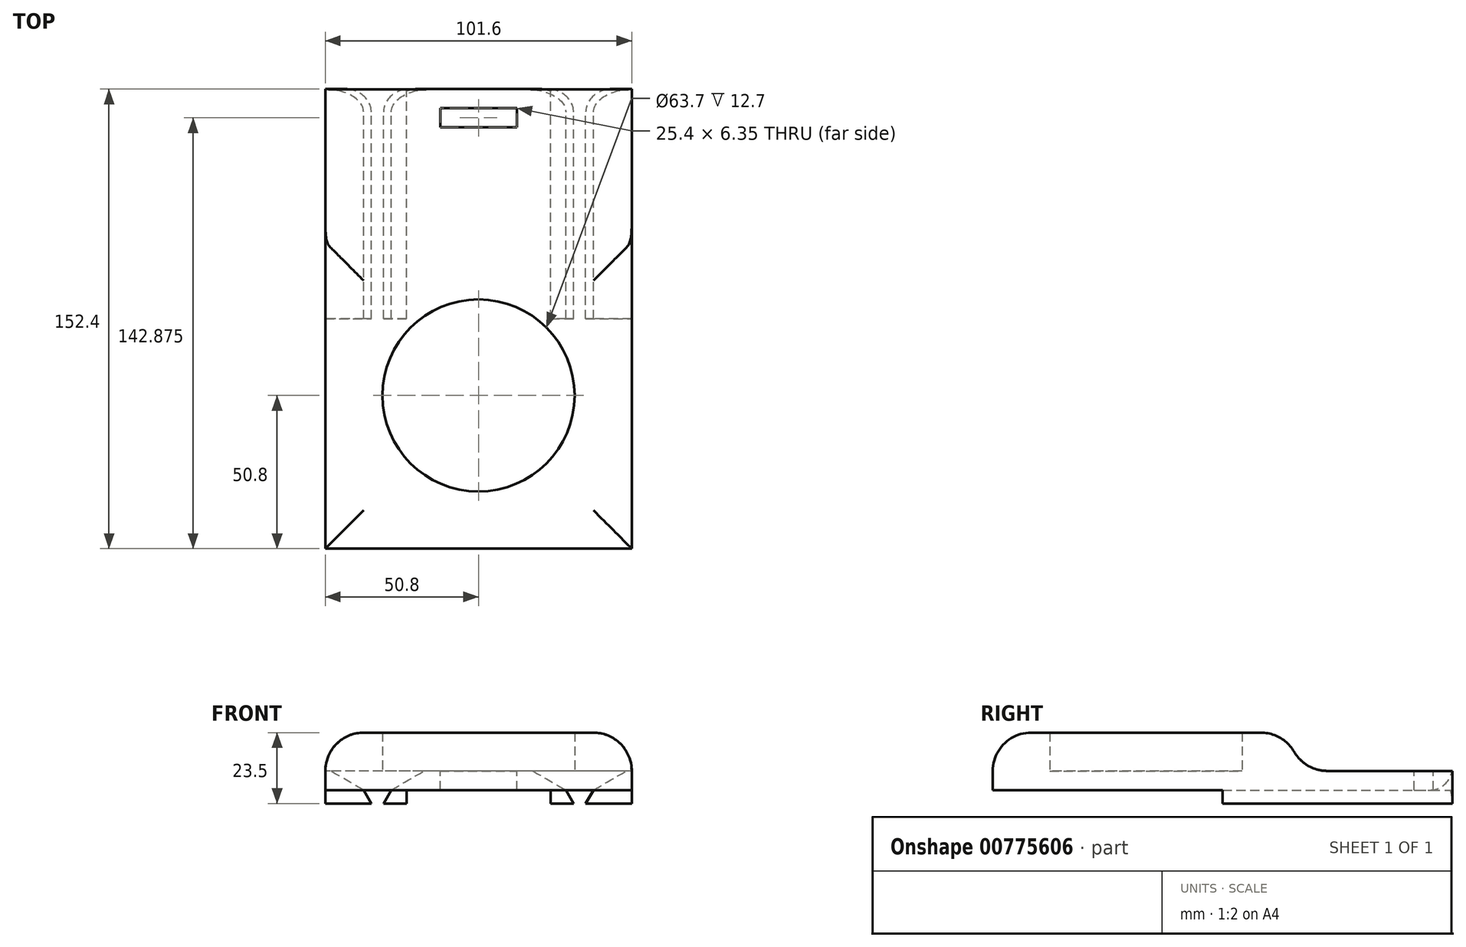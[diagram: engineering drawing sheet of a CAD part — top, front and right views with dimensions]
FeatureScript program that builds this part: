
annotation { "Feature Type Name" : "Feature", "Feature Type Description" : "" }
export const myFeature = defineFeature(function(context is Context, id is Id, definition is map)
    precondition{}
    {
        {
            var Q0;
            Q0=qCreatedBy(makeId("Top.planeOp"),FACE);
            var sketch = newSketch(context, id + "F0", { "sketchPlane" : qUnion([Q0])});
            skLineSegment(sketch, "E0.bottom", {"start": v(50.8, -76.2) * mm, "end": v(-50.8, -76.2) * mm});
            skLineSegment(sketch, "E0.top", {"start": v(50.8, 76.2) * mm, "end": v(-50.8, 76.2) * mm});
            skLineSegment(sketch, "E0.left", {"start": v(50.8, -76.2) * mm, "end": v(50.8, 76.2) * mm});
            skLineSegment(sketch, "E0.right", {"start": v(-50.8, -76.2) * mm, "end": v(-50.8, 76.2) * mm});
            skPoint(sketch, "E0.middle", {"position": v(0, 0) * mm});
            skSolve(sketch);
        }
        {
            var Q0;
            Q0 = qSketchRegion(id + "F0", true);
            extrude(context, id + "F1", {"entities" : qUnion([Q0]), "depth" : 6.35 * mm, "offsetDistance" : 25.4 * mm});
        }
        {
            var Q0;
            Q0=makeQuery(id+"F1.opExtrude","CAP_FACE",FACE,{"disambiguationData":[OSD([sQuery(id+"F0.wireOp",EDGE,"E0.bottom"),sQuery(id+"F0.wireOp",EDGE,"E0.top"),sQuery(id+"F0.wireOp",EDGE,"E0.left"),sQuery(id+"F0.wireOp",EDGE,"E0.right")])],"isStart":false});
            var sketch = newSketch(context, id + "F2", { "sketchPlane" : qUnion([Q0])});
            skLineSegment(sketch, "E1.bottom", {"start": v(-12.7, 69.85) * mm, "end": v(12.7, 69.85) * mm});
            skLineSegment(sketch, "E1.top", {"start": v(-12.7, 63.5) * mm, "end": v(12.7, 63.5) * mm});
            skLineSegment(sketch, "E1.left", {"start": v(-12.7, 69.85) * mm, "end": v(-12.7, 63.5) * mm});
            skLineSegment(sketch, "E1.right", {"start": v(12.7, 69.85) * mm, "end": v(12.7, 63.5) * mm});
            skLineSegment(sketch, "E2", {"start": v(0, -76.2) * mm, "end": v(0, 76.2) * mm});
            skSolve(sketch);
        }
        {
            var Q0;
            Q0 = qSketchRegion(id + "F2", true);
            extrude(context, id + "F3", {"entities" : qUnion([Q0]), "operationType" : NewBodyOperationType.REMOVE, "endBound" : BoundingType.UP_TO_NEXT, "oppositeDirection" : true, "depth" : 25.4 * mm, "offsetDistance" : 25.4 * mm});
        }
        {
            var Q0;
            Q0=makeQuery(id+"F1.opExtrude","SWEPT_FACE",FACE,{"disambiguationData":[OSD([sQuery(id+"F0.wireOp",EDGE,"E0.top")])]});
            var sketch = newSketch(context, id + "F4", { "sketchPlane" : qUnion([Q0])});
            skLineSegment(sketch, "E3", {"start": v(38.1, 0) * mm, "end": v(50.8, 0) * mm});
            skLineSegment(sketch, "E4", {"start": v(50.8, 0) * mm, "end": v(50.8, -4.44) * mm});
            skLineSegment(sketch, "E5", {"start": v(50.8, -4.44) * mm, "end": v(35.53, -4.44) * mm});
            skLineSegment(sketch, "E6", {"start": v(35.53, -4.45) * mm, "end": v(38.1, 0) * mm});
            skLineSegment(sketch, "E7", {"start": v(31.52, -4.44) * mm, "end": v(23.88, -4.45) * mm});
            skLineSegment(sketch, "E8", {"start": v(23.88, -4.45) * mm, "end": v(23.88, 0) * mm});
            skLineSegment(sketch, "E9", {"start": v(23.88, 0) * mm, "end": v(28.96, 0) * mm});
            skLineSegment(sketch, "E10", {"start": v(28.96, 0) * mm, "end": v(31.52, -4.45) * mm});
            skLineSegment(sketch, "E11", {"start": v(-23.88, 0) * mm, "end": v(-23.88, -4.45) * mm});
            skLineSegment(sketch, "E12", {"start": v(-23.88, -4.45) * mm, "end": v(-31.52, -4.45) * mm});
            skLineSegment(sketch, "E13", {"start": v(-31.52, -4.45) * mm, "end": v(-28.96, 0) * mm});
            skLineSegment(sketch, "E14", {"start": v(-28.96, 0) * mm, "end": v(-23.88, 0) * mm});
            skLineSegment(sketch, "E15", {"start": v(-35.53, -4.45) * mm, "end": v(-50.8, -4.45) * mm});
            skLineSegment(sketch, "E16", {"start": v(-50.8, -4.45) * mm, "end": v(-50.8, 0) * mm});
            skLineSegment(sketch, "E17", {"start": v(-50.8, 0) * mm, "end": v(-38.1, 0) * mm});
            skLineSegment(sketch, "E18", {"start": v(-38.1, 0) * mm, "end": v(-35.53, -4.45) * mm});
            skSolve(sketch);
        }
        {
            var Q0;
            Q0 = qSketchRegion(id + "F4", true);
            extrude(context, id + "F5", {"entities" : qUnion([Q0]), "operationType" : NewBodyOperationType.ADD, "oppositeDirection" : true, "depth" : 76.2 * mm, "offsetDistance" : 25.4 * mm});
        }
        {
            var Q0;
            Q0=makeQuery(id+"F5.opExtrude","CAP_EDGE",EDGE,{"disambiguationData":[OSD([sQuery(id+"F4.wireOp",EDGE,"E10")])],"isStart":true});
            var Q1;
            Q1=makeQuery(id+"F5.opExtrude","CAP_EDGE",EDGE,{"disambiguationData":[OSD([sQuery(id+"F4.wireOp",EDGE,"E6")])],"isStart":true});
            var Q2;
            {var subQ0=sQuery(id+"F4.wireOp",EDGE,"E6");var subQ1=sQuery(id+"F0.wireOp",EDGE,"E0.top");Q2=makeQuery(id+"F5.boolean.opBoolean","SPLIT",EDGE,{"disambiguationData":[TD([makeQuery(id+"F5.opExtrude","SWEPT_FACE",FACE,{"disambiguationData":[OSD([subQ0])]})])],"derivedFrom":makeQuery(id+"F1.opExtrude","CAP_EDGE",EDGE,{"disambiguationData":[OSD([subQ1])],"isStart":true})});}
            fillet(context, id + "F6", {"entities" : qUnion([Q0, Q1, Q2]), "radius" : 7.62 * mm, "tangentPropagation" : true, "allowEdgeOverflow" : false});
        }
        {
            var Q0;
            Q0=makeQuery(id+"F5.opExtrude","CAP_EDGE",EDGE,{"disambiguationData":[OSD([sQuery(id+"F4.wireOp",EDGE,"E18")])],"isStart":true});
            var Q1;
            {var subQ1=sQuery(id+"F0.wireOp",EDGE,"E0.top");var subQ2=sQuery(id+"F4.wireOp",EDGE,"E13");Q1=makeQuery(id+"F5.boolean.opBoolean","SPLIT",EDGE,{"disambiguationData":[TD([makeQuery(id+"F5.opExtrude","SWEPT_FACE",FACE,{"disambiguationData":[OSD([subQ2])]})])],"derivedFrom":makeQuery(id+"F1.opExtrude","CAP_EDGE",EDGE,{"disambiguationData":[OSD([subQ1])],"isStart":true})});}
            var Q2;
            Q2=makeQuery(id+"F5.opExtrude","CAP_EDGE",EDGE,{"disambiguationData":[OSD([sQuery(id+"F4.wireOp",EDGE,"E13")])],"isStart":true});
            fillet(context, id + "F7", {"entities" : qUnion([Q0, Q1, Q2]), "radius" : 7.62 * mm, "tangentPropagation" : true, "allowEdgeOverflow" : false});
        }
        {
            var Q0;
            Q0=makeQuery(id+"F1.opExtrude","CAP_FACE",FACE,{"disambiguationData":[OSD([sQuery(id+"F0.wireOp",EDGE,"E0.bottom"),sQuery(id+"F0.wireOp",EDGE,"E0.top"),sQuery(id+"F0.wireOp",EDGE,"E0.left"),sQuery(id+"F0.wireOp",EDGE,"E0.right")])],"isStart":false});
            var sketch = newSketch(context, id + "F8", { "sketchPlane" : qUnion([Q0])});
            skCircle(sketch, "E19", {"center": v(0, -25.4) * mm, "radius": 31.85 * mm});
            skLineSegment(sketch, "E20", {"start": v(-50.8, 25.4) * mm, "end": v(50.8, 25.4) * mm});
            skLineSegment(sketch, "E21", {"start": v(50.8, 25.4) * mm, "end": v(50.8, -76.2) * mm});
            skLineSegment(sketch, "E22", {"start": v(50.8, -76.2) * mm, "end": v(-50.8, -76.2) * mm});
            skLineSegment(sketch, "E23", {"start": v(-50.8, -76.2) * mm, "end": v(-50.8, 25.4) * mm});
            skSolve(sketch);
        }
        {
            var Q0;
            Q0 = qSketchRegion(id + "F8", true);
            extrude(context, id + "F9", {"entities" : qUnion([Q0]), "operationType" : NewBodyOperationType.ADD, "depth" : 12.7 * mm, "offsetDistance" : 25.4 * mm});
        }
        {
            var Q0;
            Q0=makeQuery(id+"F9.opExtrude","CAP_EDGE",EDGE,{"disambiguationData":[OSD([sQuery(id+"F8.wireOp",EDGE,"E23")])],"isStart":false});
            var Q1;
            Q1=makeQuery(id+"F9.opExtrude","CAP_EDGE",EDGE,{"disambiguationData":[OSD([sQuery(id+"F8.wireOp",EDGE,"E20")])],"isStart":false});
            var Q2;
            Q2=makeQuery(id+"F9.opExtrude","CAP_EDGE",EDGE,{"disambiguationData":[OSD([sQuery(id+"F8.wireOp",EDGE,"E21")])],"isStart":false});
            var Q3;
            Q3=makeQuery(id+"F9.opExtrude","CAP_EDGE",EDGE,{"disambiguationData":[OSD([sQuery(id+"F8.wireOp",EDGE,"E22")])],"isStart":false});
            fillet(context, id + "F10", {"entities" : qUnion([Q0, Q1, Q2, Q3]), "radius" : 12.7 * mm, "tangentPropagation" : true, "allowEdgeOverflow" : false});
        }
        {
            var Q0;
            {var subQ4=sQuery(id+"F0.wireOp",EDGE,"E0.top");var subQ5=sQuery(id+"F0.wireOp",EDGE,"E0.left");var subQ7=sQuery(id+"F0.wireOp",EDGE,"E0.right");var subQ8=sQuery(id+"F8.wireOp",EDGE,"E20");Q0=makeQuery(id+"F10.opFillet","BLEND_EDGE",EDGE,{"blendedFrom":[makeQuery(id+"F9.opExtrude","CAP_EDGE",EDGE,{"disambiguationData":[OSD([subQ8])],"isStart":false}),makeQuery(id+"F9.boolean.opBoolean","SPLIT",FACE,{"disambiguationData":[TD([makeQuery(id+"F1.opExtrude","SWEPT_FACE",FACE,{"disambiguationData":[OSD([subQ4])]})])],"derivedFrom":makeQuery(id+"F1.opExtrude","CAP_FACE",FACE,{"disambiguationData":[OSD([sQuery(id+"F0.wireOp",EDGE,"E0.bottom"),subQ4,subQ5,subQ7])],"isStart":false})})],"blendedInto":[makeQuery(id+"F9.boolean.opBoolean","SPLIT",FACE,{"disambiguationData":[TD([makeQuery(id+"F1.opExtrude","SWEPT_FACE",FACE,{"disambiguationData":[OSD([subQ4])]})])],"derivedFrom":makeQuery(id+"F1.opExtrude","CAP_FACE",FACE,{"disambiguationData":[OSD([sQuery(id+"F0.wireOp",EDGE,"E0.bottom"),subQ4,subQ5,subQ7])],"isStart":false})})]});}
            fillet(context, id + "F11", {"entities" : qUnion([Q0]), "radius" : 12.7 * mm, "tangentPropagation" : true, "allowEdgeOverflow" : false});
        }
    });
